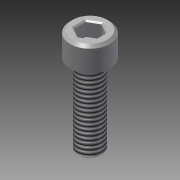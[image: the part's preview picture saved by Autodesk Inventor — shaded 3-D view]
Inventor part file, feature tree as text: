
AUTODESK INVENTOR PART (.ipt)
format: ipt  version: 2013 (Build 170138000, 138)  size: 91,648 bytes
history: native  units: in
note: dims shown in document units (in); Inventor stores cm internally (conversion verified against a paired STEP export)
features: other x2, thread x1, imported_body x1
ambient origin geometry x8: Origin, YZ Plane, XZ Plane, XY Plane, X Axis, Y Axis, Z Axis, Center Point
feature tree (4):
  other  "10-32x0625_shcs"
  other  "10-32x0625_shcs1"
  thread  "Thread1"  [1 undecoded]
  imported_body  "Base1"
note: 1 required parameter value undecoded (feature->parameter linkage not recoverable at this tier; creation-order binding heuristic only, values carry confidence <= 0.55)
